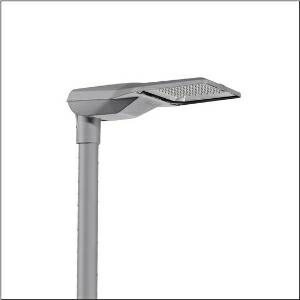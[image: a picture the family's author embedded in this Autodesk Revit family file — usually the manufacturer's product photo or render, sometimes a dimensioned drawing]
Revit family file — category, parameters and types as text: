
# Revit family: streetlight_sl_21_iq_midi___pl52_5xe3h31d08mb_2c0b
name_source: partatom
category: Lighting Fixtures
units: mm (PartAtom-declared; Revit-internal decimal feet)

## family parameters
Cut with Voids When Loaded = No
Host = Face
Light Source = No
Part Type = Normal
Room Calculation Point = No
Round Connector Dimension = Use Diameter
Shared = No

## types (1)
- --- (1 x LED, 19170 lm, 146.7 W, 3000K)
    Apparent Load = 147 VA
    CIE Flux Codes = 27 59 98 100 100
    Color Rendering = 70
    Color Temperature = 3000K
    Default Elevation = 1800 mm
    Description = Streetlight SL 21 iQ midi, mast luminaire, primary light control with lens, of PMMA, primary optical cover: cover, of toughened safety glass, transparent, light distribution: PL52, light emission: direct distribution, primary light characteristic: asymmetric, installation type: post-top, side-entry, LED, High Power LED, rated luminous flux: 19.170lm, luminous efficacy: 131lm/W, light colour: 730, colour temperature: 3000K, control gear: iQ-Comfort, control: Auto-Match, Temp-Guard, Lumen-Switch, Night-Set, Smart-Wire, Light-Fading, Desk-Remote (wireless, voltage-free reading and setting of iQ features in the workshop via application-optimized NFC function/RFID function), optimised constant luminous flux control (CLO 2.0), pre-setting: linear dimming characteristic, mains connection: 230..240V, AC, 50/60Hz, start of lifetime: 147W, end of service life: 161W, reduction: 62W, luminaire housing, of diecast aluminium, powder-coated, Siteco® metallic grey (DB 702S), corrosivity category C5 mid according to DIN EN ISO 12944, please order mast flange separately, inclination adjustable: 0°, 5°, 10°, 15°, sealing non-destructively replaceable, multi-level sealing system, length: 644mm, width: 335mm, height: 110mm, mast flange for spigot size: 42mm (side-entry): 5XC10008XM4, 60/48mm (side-entry/post-top): 5XC10108XM2, 76/60mm (side-entry/post-top): 5XC10108XM1, mounting height: 4..8m, protection rating (complete): IP66, insulation class (complete): insulation class II (safety insulation), certification: CE, ENEC, ENEC+, VDE, impact resistance: IK10, permissible operating ambient temperature for outdoor applications: -40..+50°C, standard-compliant lighting for roads and squares, packaging unit: 1 piece

Light Distribution: PL52
    Height = 111 mm
    Lamp = 1 x LED
    Lamp Light Flux = 19170 lm
    Lamp Power = 146.7 W
    Lamp count = 1
    Length = 644 mm
    Luminous efficacy = 131 lm/W
    Manufacturer = Siteco
    ModVariant = No
    Model = 5XE3H31D08MB
    Number of Poles = 1
    OnlyDefault = Yes
    Power Factor = 1
    Product Name = Streetlight SL 21 iQ midi | PL52
    Product group = mast luminaire | pylon top
    ProductGroupID = 6100
    Protection Class = Protection class II
    Protection Degree = IP 66
    RLX_Detail_Level = 1
    RLX_Emergency_Light_Flux = 0 lm
    RLX_Emergency_Type = 0
    RLX_Emergency_Type_DB = No
    RlxData = <blob elided: 36569 chars, md5=0811e379>
    Socket = socket
    Standby Power = 0 W
    System Light Flux = 19169 lm
    System Power = 147 W
    Type Comments = factory setting: luminous flux: 100 % | dim-lin: 254 | 753 mA
    Type Image = l_1004298.jpg
    URL = http://relux.com
    VarID = @adj_212117
    Voltage = 0 V
    Weight = 0.00 kg
    Width = 336 mm

## geometry (parser evidence)
native form markers: Blend x4, Sweep x11
no freeform markers — native parametric forms only
